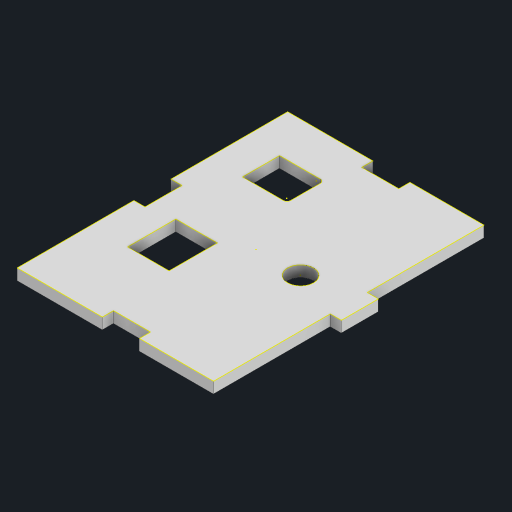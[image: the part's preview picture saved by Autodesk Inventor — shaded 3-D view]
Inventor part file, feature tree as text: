
AUTODESK INVENTOR PART (.ipt)
format: ipt  version: 2023 (Build 270158000, 158)  size: 200,704 bytes
history: native  units: mm
features: reference x9, extrude x6, sketch x6, other x6, projected_geometry x1
ambient origin geometry x8: Origin, YZ Plane, XZ Plane, XY Plane, X Axis, Y Axis, Z Axis, Center Point
bodies: Solid1 (feature_tree)
feature tree (28):
  extrude  "Extrusion1"  Depth=56.0mm
  extrude  "Extrusion3"  TaperAngle=0.0deg  [1 undecoded]
  extrude  "Extrusion4"  Depth=16.0mm
  extrude  "Extrusion7"  Depth=10.0mm
  sketch  "Sketch9"  dims[d27=3.0mm d28=10.0mm]
  extrude  "Extrusion8"  Depth=10.0mm
  extrude  "Extrusion9"  Depth=3.0mm
  sketch  "Sketch10"  dims[d29=3.0mm d30=3.0mm d31=10.0mm d32=3.0mm d33=10.0mm d34=0.0mm d35=0.0mm d36=36.5mm d38=0.5mm d39=0.5mm d41=3.0mm d42=0.0mm d43=0.0mm d44=0.0mm]
  sketch  "Sketch1"  dims[d0=73.0mm d1=56.0mm]
  sketch  "Sketch3"  dims[d2=3.0mm d3=0.0mm d10=0.0mm d11=0.0mm]
  sketch  "Sketch4"  dims[d12=7.0mm d13=16.0mm]
  sketch  "Sketch7"  dims[d14=0.0mm d15=0.0mm d26=10.0mm]
  reference  "Reference14"
  reference  "Reference15"
  reference  "Reference16"
  reference  "Reference17"
  reference  "Reference18"
  reference  "Reference19"
  reference  "Reference20"
  reference  "Reference21"
  reference  "Reference22"
  parser-record x1  (decoder bookkeeping rows leaked as tree rows — omitted from the tree; the rows remain in map.json)
  other  "AlarmClock.iam"
  other  "arduino uno:1"
  other  "USB type b.SLDPRT_3"
  other  "USB SHELL_82"
  other  "power jack_4"
  projected_geometry  "Project Cut Edges1"
note: 1 required parameter value undecoded (feature->parameter linkage not recoverable at this tier; creation-order binding heuristic only, values carry confidence <= 0.55)
note: 1 file-system path scrubbed to <path> (originals preserved in map.json)
